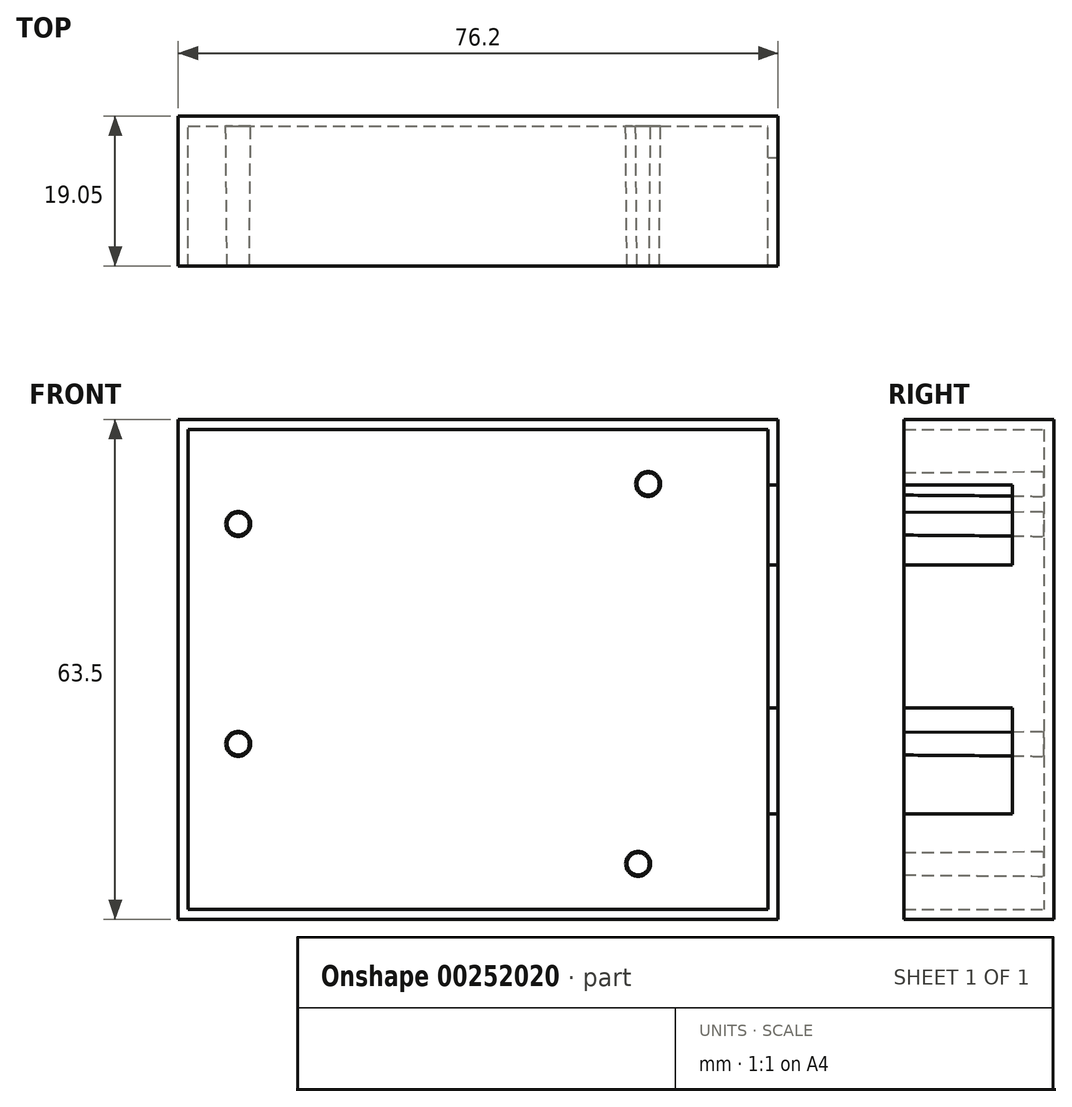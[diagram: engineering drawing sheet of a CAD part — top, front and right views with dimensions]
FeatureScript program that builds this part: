
annotation { "Feature Type Name" : "Feature", "Feature Type Description" : "" }
export const myFeature = defineFeature(function(context is Context, id is Id, definition is map)
    precondition{}
    {
        {
            var Q0;
            Q0=qCreatedBy(makeId("Front.planeOp"),FACE);
            var sketch = newSketch(context, id + "F0", { "sketchPlane" : qUnion([Q0])});
            skLineSegment(sketch, "E0.bottom", {"start": v(0, 63.5) * mm, "end": v(76.2, 63.5) * mm});
            skLineSegment(sketch, "E0.top", {"start": v(0, 0) * mm, "end": v(76.2, 0) * mm});
            skLineSegment(sketch, "E0.left", {"start": v(0, 63.5) * mm, "end": v(0, 0) * mm});
            skLineSegment(sketch, "E0.right", {"start": v(76.2, 63.5) * mm, "end": v(76.2, 0) * mm});
            skSolve(sketch);
        }
        {
            var Q0;
            Q0=makeQuery(id+"F0.imprint","IMPRINT",FACE,{"disambiguationData":[TD([[makeQuery(id+"F0.imprint","IMPRINT",EDGE,{"derivedFrom":sQuery(id+"F0.wireOp",EDGE,"brBC3KbL-EG9J-vsdL-SePl-hzVDqoBTHbGP")}),1.0]])]});
            var Q1;
            Q1=makeQuery(id+"F0.imprint","IMPRINT",FACE,{"disambiguationData":[TD([[makeQuery(id+"F0.imprint","IMPRINT",EDGE,{"derivedFrom":sQuery(id+"F0.wireOp",EDGE,"BntW7quv-2HLz-dvJl-wQES-wXUxCfIMOkLv")}),1.0]])]});
            var Q2;
            Q2=makeQuery(id+"F0.imprint","IMPRINT",FACE,{"disambiguationData":[TD([[makeQuery(id+"F0.imprint","IMPRINT",EDGE,{"derivedFrom":sQuery(id+"F0.wireOp",EDGE,"aSzLEpmf-ETZK-BwI2-V2vw-FS7RvumS7vd2")}),1.0]])]});
            var Q3;
            Q3=makeQuery(id+"F0.imprint","IMPRINT",FACE,{"disambiguationData":[TD([[makeQuery(id+"F0.imprint","IMPRINT",EDGE,{"derivedFrom":sQuery(id+"F0.wireOp",EDGE,"Ap6Lo27P-b6BO-CC3j-8LaT-OWlvdygEvpYj")}),1.0]])]});
            var Q4;
            Q4=makeQuery(id+"F0.imprint","IMPRINT",FACE,{"disambiguationData":[TD([[makeQuery(id+"F0.imprint","IMPRINT",EDGE,{"derivedFrom":sQuery(id+"F0.wireOp",EDGE,"E0.bottom")}),-1.0]])]});
            extrude(context, id + "F1", {"entities" : qUnion([Q0, Q1, Q2, Q3, Q4]), "depth" : 19.05 * mm});
        }
        {
            var Q0;
            Q0=makeQuery(id+"F0.imprint","IMPRINT",FACE,{"disambiguationData":[TD([[makeQuery(id+"F0.imprint","IMPRINT",EDGE,{"derivedFrom":sQuery(id+"F0.wireOp",EDGE,"E0.bottom")}),-1.0]])]});
            var sketch = newSketch(context, id + "F2", { "sketchPlane" : qUnion([Q0])});
            skCircle(sketch, "E1", {"center": v(59.69, 55.32) * mm, "radius": 1.59 * mm});
            skCircle(sketch, "E2", {"center": v(7.62, 50.24) * mm, "radius": 1.59 * mm});
            skCircle(sketch, "E3", {"center": v(7.62, 22.3) * mm, "radius": 1.59 * mm});
            skCircle(sketch, "E4", {"center": v(58.42, 7.06) * mm, "radius": 1.59 * mm});
            skSolve(sketch);
        }
        {
            var Q0;
            Q0=makeQuery(id+"F1.opExtrude","CAP_FACE",FACE,{"disambiguationData":[OSD([sQuery(id+"F0.wireOp",EDGE,"E0.bottom"),sQuery(id+"F0.wireOp",EDGE,"E0.top"),sQuery(id+"F0.wireOp",EDGE,"E0.left"),sQuery(id+"F0.wireOp",EDGE,"E0.right")])],"isStart":false});
            var Q1;
            Q1=makeQuery(id+"F1.opExtrude","SWEPT_BODY",BODY,{"disambiguationData":[OSD([sQuery(id+"F0.wireOp",EDGE,"E0.bottom"),sQuery(id+"F0.wireOp",EDGE,"E0.top"),sQuery(id+"F0.wireOp",EDGE,"E0.left"),sQuery(id+"F0.wireOp",EDGE,"E0.right")])]});
            shell(context, id + "F3", {"entities" : qUnion([Q0]), "parts" : qUnion([Q1]), "thickness" : 1.27 * mm});
        }
        {
            var Q0;
            Q0 = qSketchRegion(id + "F2", true);
            extrude(context, id + "F4", {"entities" : qUnion([Q0]), "operationType" : NewBodyOperationType.ADD, "depth" : 19.05 * mm, "hasDraft" : true, "draftAngle" : .5 * degree, "draftPullDirection" : true});
        }
        {
            var Q0;
            Q0=makeQuery(id+"F1.opExtrude","SWEPT_FACE",FACE,{"disambiguationData":[OSD([sQuery(id+"F0.wireOp",EDGE,"E0.right")])]});
            var sketch = newSketch(context, id + "F5", { "sketchPlane" : qUnion([Q0])});
            skLineSegment(sketch, "E5.bottom", {"start": v(-19.27, 26.86) * mm, "end": v(-5.3, 26.86) * mm});
            skLineSegment(sketch, "E5.top", {"start": v(-19.27, 13.4) * mm, "end": v(-5.3, 13.4) * mm});
            skLineSegment(sketch, "E5.left", {"start": v(-19.27, 26.86) * mm, "end": v(-19.27, 13.4) * mm});
            skLineSegment(sketch, "E5.right", {"start": v(-5.3, 26.86) * mm, "end": v(-5.3, 13.4) * mm});
            skLineSegment(sketch, "E6.bottom", {"start": v(-19.27, 55.2) * mm, "end": v(-5.3, 55.2) * mm});
            skLineSegment(sketch, "E6.top", {"start": v(-19.27, 45.04) * mm, "end": v(-5.3, 45.04) * mm});
            skLineSegment(sketch, "E6.left", {"start": v(-19.27, 55.2) * mm, "end": v(-19.27, 45.04) * mm});
            skLineSegment(sketch, "E6.right", {"start": v(-5.3, 55.2) * mm, "end": v(-5.3, 45.04) * mm});
            skSolve(sketch);
        }
        {
            var Q0;
            Q0=makeQuery(id+"F5.imprint","IMPRINT",FACE,{"disambiguationData":[TD([[makeQuery(id+"F5.imprint","IMPRINT",EDGE,{"derivedFrom":sQuery(id+"F5.wireOp",EDGE,"E6.bottom")}),-1.0]])]});
            var Q1;
            Q1=makeQuery(id+"F5.imprint","IMPRINT",FACE,{"disambiguationData":[TD([[makeQuery(id+"F5.imprint","IMPRINT",EDGE,{"derivedFrom":sQuery(id+"F5.wireOp",EDGE,"E5.bottom")}),-1.0]])]});
            extrude(context, id + "F6", {"entities" : qUnion([Q0, Q1]), "operationType" : NewBodyOperationType.REMOVE, "oppositeDirection" : true, "depth" : 1.27 * mm});
        }
    });
